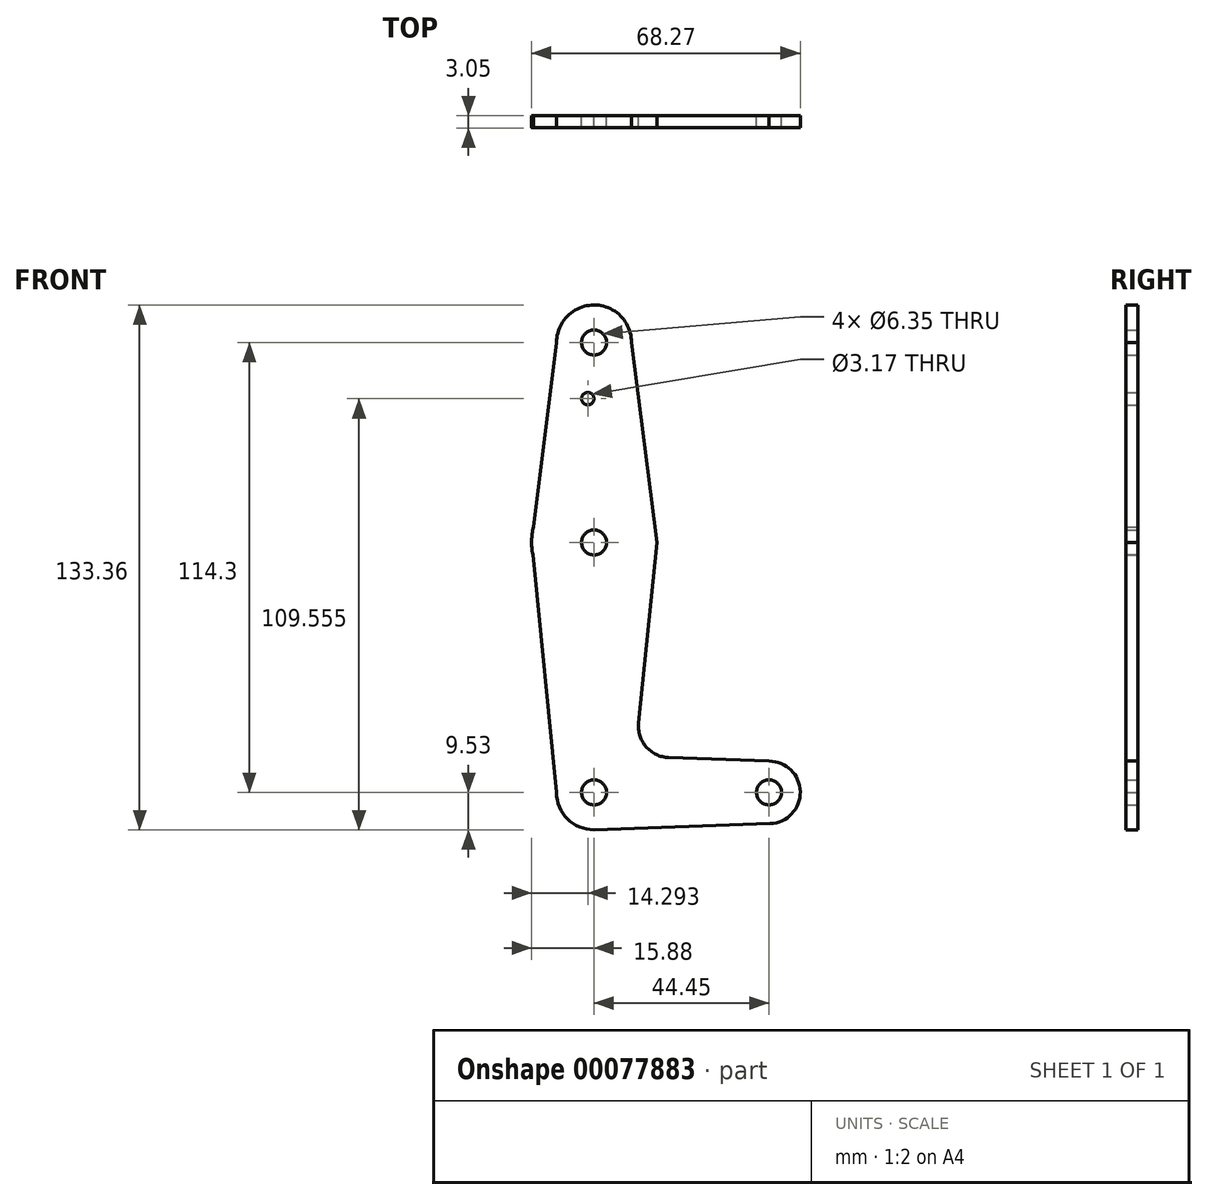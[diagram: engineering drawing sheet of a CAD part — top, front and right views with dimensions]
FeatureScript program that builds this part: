
annotation { "Feature Type Name" : "Feature", "Feature Type Description" : "" }
export const myFeature = defineFeature(function(context is Context, id is Id, definition is map)
    precondition{}
    {
        {
            var Q0;
            Q0=qCreatedBy(makeId("Front.planeOp"),FACE);
            var sketch = newSketch(context, id + "F0", { "sketchPlane" : qUnion([Q0])});
            skLineSegment(sketch, "E0", {"start": v(0, 0) * mm, "end": v(0, 114.3) * mm, "construction": true});
            skLineSegment(sketch, "E1", {"start": v(0, 0) * mm, "end": v(44.45, 0) * mm, "construction": true});
            skPoint(sketch, "E2", {"position": v(44.45, 0) * mm});
            skCircle(sketch, "E3", {"center": v(44.45, 0) * mm, "radius": 7.94 * mm});
            skPoint(sketch, "E4", {"position": v(0, 0) * mm});
            skCircle(sketch, "E5", {"center": v(0, 0) * mm, "radius": 9.53 * mm});
            skPoint(sketch, "E6", {"position": v(0, 49.56) * mm});
            skCircle(sketch, "E7", {"center": v(0, 114.3) * mm, "radius": 9.53 * mm});
            skLineSegment(sketch, "E8", {"start": v(0, 0) * mm, "end": v(0, 63.5) * mm, "construction": true});
            skCircle(sketch, "E9", {"center": v(0, 63.5) * mm, "radius": 15.88 * mm});
            skLineSegment(sketch, "E10", {"start": v(9.53, 114.3) * mm, "end": v(16, 63.5) * mm});
            skLineSegment(sketch, "E11", {"start": v(16, 63.5) * mm, "end": v(11.32, 17.6) * mm});
            skLineSegment(sketch, "E12", {"start": v(-9.53, 0) * mm, "end": v(-15.87, 63.47) * mm});
            skLineSegment(sketch, "E13", {"start": v(-15.87, 63.47) * mm, "end": v(-9.52, 114.23) * mm});
            skLineSegment(sketch, "E14", {"start": v(18.95, 8.85) * mm, "end": v(44.45, 7.94) * mm});
            skLineSegment(sketch, "E15", {"start": v(0, -9.53) * mm, "end": v(44.73, -7.93) * mm});
            skArc(sketch, "E16.filletArc", {"start": v(11.32, 17.6) * mm, "mid": v(13.24, 11.57) * mm, "end": v(18.95, 8.85) * mm});
            skCircle(sketch, "E17", {"center": v(0, 114.3) * mm, "radius": 3.18 * mm});
            skCircle(sketch, "E18", {"center": v(0, 63.5) * mm, "radius": 3.18 * mm});
            skCircle(sketch, "E19", {"center": v(0, 0) * mm, "radius": 3.18 * mm});
            skCircle(sketch, "E20", {"center": v(44.45, 0) * mm, "radius": 3.18 * mm});
            skCircle(sketch, "E21", {"center": v(-1.59, 100.03) * mm, "radius": 1.59 * mm});
            skSolve(sketch);
        }
        {
            var Q0;
            {var subQ0=sQuery(id+"F0.wireOp",EDGE,"E15");var subQ1=sQuery(id+"F0.wireOp",EDGE,"E5");var subQ2=makeQuery(id+"F0.imprint","INTERSECT",VERTEX,{"disambiguationData":[OD(0.0)],"derivedFrom":[subQ1,subQ0]});Q0=makeQuery(id+"F0.imprint","IMPRINT",FACE,{"disambiguationData":[TD([[makeQuery(id+"F0.imprint","IMPRINT",EDGE,{"disambiguationData":[TD([[subQ2,-1.0]])],"derivedFrom":subQ1}),1.0]])]});}
            var Q1;
            {var subQ0=sQuery(id+"F0.wireOp",EDGE,"E13");var subQ1=sQuery(id+"F0.wireOp",EDGE,"E9");var subQ3=makeQuery(id+"F0.imprint","INTERSECT",VERTEX,{"derivedFrom":[subQ1,subQ0]});Q1=makeQuery(id+"F0.imprint","IMPRINT",FACE,{"disambiguationData":[TD([[makeQuery(id+"F0.imprint","IMPRINT",EDGE,{"disambiguationData":[TD([[subQ3,-1.0]])],"derivedFrom":subQ1}),1.0]])]});}
            var Q2;
            {var subQ0=sQuery(id+"F0.wireOp",EDGE,"E12");var subQ1=sQuery(id+"F0.wireOp",EDGE,"E9");var subQ3=makeQuery(id+"F0.imprint","INTERSECT",VERTEX,{"derivedFrom":[subQ1,subQ0]});Q2=makeQuery(id+"F0.imprint","IMPRINT",FACE,{"disambiguationData":[TD([[makeQuery(id+"F0.imprint","IMPRINT",EDGE,{"disambiguationData":[TD([[subQ3,1.0]])],"derivedFrom":subQ1}),1.0]])]});}
            var Q3;
            Q3=makeQuery(id+"F0.imprint","IMPRINT",FACE,{"disambiguationData":[TD([[makeQuery(id+"F0.imprint","IMPRINT",EDGE,{"derivedFrom":sQuery(id+"F0.wireOp",EDGE,"E20")}),-1.0]])]});
            var Q4;
            Q4=makeQuery(id+"F0.imprint","IMPRINT",FACE,{"disambiguationData":[TD([[makeQuery(id+"F0.imprint","IMPRINT",EDGE,{"derivedFrom":sQuery(id+"F0.wireOp",EDGE,"E17")}),-1.0]])]});
            var Q5;
            {var subQ0=sQuery(id+"F0.wireOp",EDGE,"E11");Q5=makeQuery(id+"F0.imprint","IMPRINT",FACE,{"disambiguationData":[TD([[makeQuery(id+"F0.imprint","IMPRINT",EDGE,{"derivedFrom":subQ0}),-1.0]])]});}
            var Q6;
            Q6=makeQuery(id+"F0.imprint","IMPRINT",FACE,{"disambiguationData":[TD([[makeQuery(id+"F0.imprint","IMPRINT",EDGE,{"derivedFrom":sQuery(id+"F0.wireOp",EDGE,"E19")}),-1.0]])]});
            var Q7;
            Q7=makeQuery(id+"F0.imprint","IMPRINT",FACE,{"disambiguationData":[TD([[makeQuery(id+"F0.imprint","IMPRINT",EDGE,{"derivedFrom":sQuery(id+"F0.wireOp",EDGE,"E21")}),-1.0]])]});
            var Q8;
            Q8=makeQuery(id+"F0.imprint","IMPRINT",FACE,{"disambiguationData":[TD([[makeQuery(id+"F0.imprint","IMPRINT",EDGE,{"derivedFrom":sQuery(id+"F0.wireOp",EDGE,"E18")}),-1.0]])]});
            extrude(context, id + "F1", {"entities" : qUnion([Q0, Q1, Q2, Q3, Q4, Q5, Q6, Q7, Q8]), "depth" : 3.05 * mm});
        }
    });
